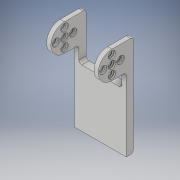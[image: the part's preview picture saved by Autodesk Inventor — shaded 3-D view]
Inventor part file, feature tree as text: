
AUTODESK INVENTOR PART (.ipt)
format: ipt  version: 2018 (Build 220112000, 112)  size: 241,664 bytes
history: native  units: in
note: dims shown in document units (in); Inventor stores cm internally (conversion verified against a paired STEP export)
features: extrude x5, sketch x5, chamfer x2, plane x2, pattern_linear x2, mirror x1, fillet x1
ambient origin geometry x8: Origin, YZ Plane, XZ Plane, XY Plane, X Axis, Y Axis, Z Axis, Center Point
bodies: Solid1 (feature_tree)
feature tree (18):
  extrude  "Extrusion1"  Depth=0.1969in
  extrude  "Extrusion2"  Depth=0.0787in
  extrude  "Extrusion3"  Depth=0.0787in
  extrude  "Extrusion4"  Depth=0.1181in
  chamfer  "Chamfer1"  Distance=0.1181in
  chamfer  "Chamfer2"  Distance=0.0394in
  plane  "Work Plane1"
  pattern_linear  "Rectangular Pattern1"  Spacing1=0.2047in  [1 undecoded]
  pattern_linear  "Rectangular Pattern2"  Spacing1=0.0394in  [1 undecoded]
  extrude  "Extrusion5"  Depth=0.0787in TaperAngle=45.0deg
  mirror  "Mirror1"
  fillet  "Fillet1"  Radius=0.0787in
  sketch  "Sketch1"  dims[d0=0.748in d4=0.1969in]
  sketch  "Sketch2"  dims[d6=2.185in d8=0.0787in]
  sketch  "Sketch3"  dims[d9=0.0787in d10=0.0787in]
  sketch  "Sketch4"  dims[d11=0.1181in d12=0.0in d13=0.1614in d14=0.1181in d15=0.0in]
  sketch  "Sketch5"  dims[d16=0.2047in d17=0.0394in d18=0.0in d19=0.2047in d20=0.0394in d21=0.0in d22=0.0217in d23=0.0787in d24=45.0deg d25=0.0217in d26=0.0787in d27=45.0deg d28=0.7874in d30=0.2362in d31=0.7874in d33=0.2362in d34=0.7874in d36=0.2362in d37=0.7874in d39=0.2362in d40=1.5748in d41=0.0787in d42=0.5906in d43=0.0in d44=0.0787in]
  plane  "Work Plane2"
note: 2 required parameter values undecoded (feature->parameter linkage not recoverable at this tier; creation-order binding heuristic only, values carry confidence <= 0.55)
